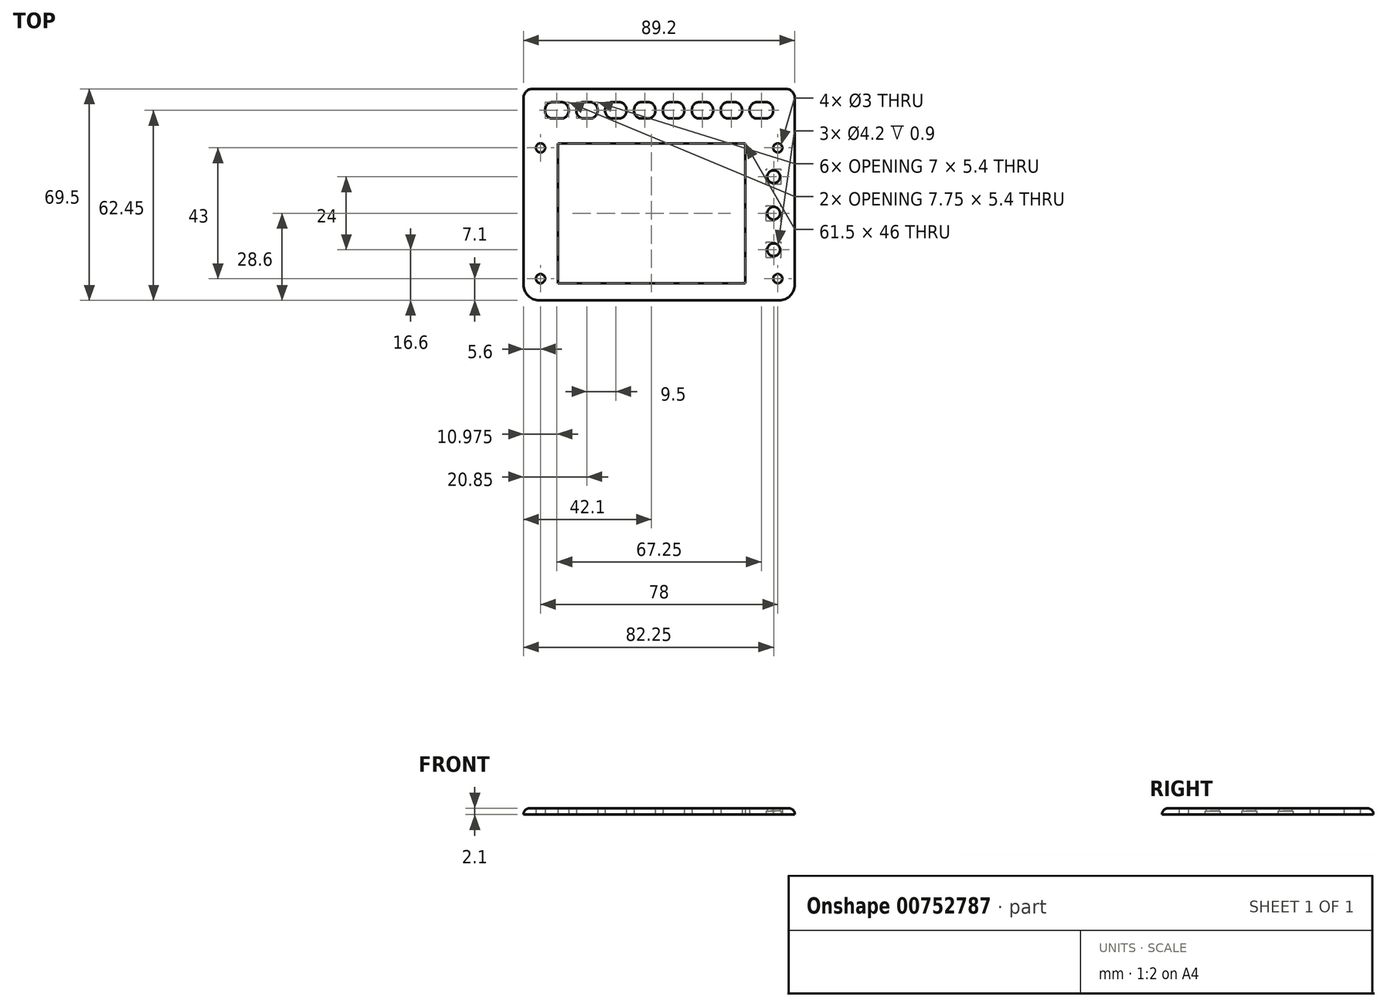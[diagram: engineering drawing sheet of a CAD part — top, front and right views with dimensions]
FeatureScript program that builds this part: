
annotation { "Feature Type Name" : "Feature", "Feature Type Description" : "" }
export const myFeature = defineFeature(function(context is Context, id is Id, definition is map)
    precondition{}
    {
        {
            var Q0;
            Q0=qCreatedBy(makeId("Top.planeOp"),FACE);
            var sketch = newSketch(context, id + "F0", { "sketchPlane" : qUnion([Q0])});
            skLineSegment(sketch, "E0.bottom", {"start": v(-39.5, 26.5) * mm, "end": v(39.5, 26.5) * mm});
            skLineSegment(sketch, "E0.top", {"start": v(-39.5, -26.5) * mm, "end": v(39.5, -26.5) * mm});
            skLineSegment(sketch, "E0.left", {"start": v(-42.5, 23.5) * mm, "end": v(-42.5, -23.5) * mm});
            skLineSegment(sketch, "E0.right", {"start": v(42.5, 23.5) * mm, "end": v(42.5, -23.5) * mm});
            skPoint(sketch, "E0.middle", {"position": v(0, 0) * mm});
            skLineSegment(sketch, "E1.bottom", {"start": v(-39, 21.5) * mm, "end": v(39, 21.5) * mm, "construction": true});
            skLineSegment(sketch, "E1.top", {"start": v(-39, -21.5) * mm, "end": v(39, -21.5) * mm, "construction": true});
            skLineSegment(sketch, "E1.left", {"start": v(-39, 21.5) * mm, "end": v(-39, -21.5) * mm, "construction": true});
            skLineSegment(sketch, "E1.right", {"start": v(39, 21.5) * mm, "end": v(39, -21.5) * mm, "construction": true});
            skCircle(sketch, "E2", {"center": v(-39, 21.5) * mm, "radius": 1.5 * mm});
            skCircle(sketch, "E3", {"center": v(39, 21.5) * mm, "radius": 1.5 * mm});
            skCircle(sketch, "E4", {"center": v(39, -21.5) * mm, "radius": 1.5 * mm});
            skCircle(sketch, "E5", {"center": v(-39, -21.5) * mm, "radius": 1.5 * mm});
            skPoint(sketch, "E6.visualSharp", {"position": v(-42.5, 26.5) * mm});
            skArc(sketch, "E6.filletArc", {"start": v(-39.5, 26.5) * mm, "mid": v(-41.62, 25.62) * mm, "end": v(-42.5, 23.5) * mm});
            skPoint(sketch, "E7.visualSharp", {"position": v(42.5, 26.5) * mm});
            skArc(sketch, "E7.filletArc", {"start": v(42.5, 23.5) * mm, "mid": v(41.62, 25.62) * mm, "end": v(39.5, 26.5) * mm});
            skPoint(sketch, "E8.visualSharp", {"position": v(42.5, -26.5) * mm});
            skArc(sketch, "E8.filletArc", {"start": v(39.5, -26.5) * mm, "mid": v(41.62, -25.62) * mm, "end": v(42.5, -23.5) * mm});
            skPoint(sketch, "E9.visualSharp", {"position": v(-42.5, -26.5) * mm});
            skArc(sketch, "E9.filletArc", {"start": v(-42.5, -23.5) * mm, "mid": v(-41.62, -25.62) * mm, "end": v(-39.5, -26.5) * mm});
            skLineSegment(sketch, "E10", {"start": v(0, 0) * mm, "end": v(-35, 0) * mm, "construction": true});
            skLineSegment(sketch, "E11", {"start": v(-35, 26.5) * mm, "end": v(-35, -26.5) * mm});
            skLineSegment(sketch, "E12", {"start": v(0, 0) * mm, "end": v(0, 23) * mm, "construction": true});
            skLineSegment(sketch, "E13.MirrorCS", {"start": v(35, 26.5) * mm, "end": v(35, -26.5) * mm});
            skLineSegment(sketch, "E14.1", {"start": v(-44.6, 23.5) * mm, "end": v(-44.6, -23.5) * mm});
            skLineSegment(sketch, "E14.2", {"start": v(-39.5, 28.6) * mm, "end": v(39.5, 28.6) * mm});
            skArc(sketch, "E14.3", {"start": v(-44.6, -23.5) * mm, "mid": v(-43.1, -27.1) * mm, "end": v(-39.5, -28.6) * mm});
            skLineSegment(sketch, "E14.5", {"start": v(44.6, 23.5) * mm, "end": v(44.6, -23.5) * mm});
            skArc(sketch, "E14.6", {"start": v(39.5, -28.6) * mm, "mid": v(43.1, -27.1) * mm, "end": v(44.6, -23.5) * mm});
            skLineSegment(sketch, "E14.7", {"start": v(-39.5, -28.6) * mm, "end": v(39.5, -28.6) * mm});
            skLineSegment(sketch, "E15", {"start": v(-42.5, 0) * mm, "end": v(-44.6, 0) * mm, "construction": true});
            skLineSegment(sketch, "E16.bottom", {"start": v(-44.6, 9) * mm, "end": v(-42.5, 9) * mm});
            skLineSegment(sketch, "E16.top", {"start": v(-44.6, -9) * mm, "end": v(-42.5, -9) * mm});
            skLineSegment(sketch, "E16.left", {"start": v(-44.6, 9) * mm, "end": v(-44.6, -9) * mm});
            skLineSegment(sketch, "E16.right", {"start": v(-42.5, 9) * mm, "end": v(-42.5, -9) * mm});
            skPoint(sketch, "E16.middle", {"position": v(-43.55, 0) * mm});
            skLineSegment(sketch, "E17", {"start": v(-42.5, 9) * mm, "end": v(-35, 9) * mm});
            skLineSegment(sketch, "E18", {"start": v(-42.5, -9) * mm, "end": v(-35, -9) * mm});
            skLineSegment(sketch, "E19", {"start": v(0, 28.6) * mm, "end": v(0, 39.1) * mm, "construction": true});
            skLineSegment(sketch, "E20", {"start": v(0, 39.1) * mm, "end": v(-39.5, 39.1) * mm});
            skLineSegment(sketch, "E21", {"start": v(0, 39.1) * mm, "end": v(39.5, 39.1) * mm});
            skLineSegment(sketch, "E22.0", {"start": v(0, 40.9) * mm, "end": v(41.6, 40.9) * mm});
            skLineSegment(sketch, "E22.1", {"start": v(0, 40.9) * mm, "end": v(-41.6, 40.9) * mm});
            skLineSegment(sketch, "E23", {"start": v(-42.5, 23.5) * mm, "end": v(-42.5, 36.1) * mm});
            skLineSegment(sketch, "E24", {"start": v(42.5, 23.5) * mm, "end": v(42.5, 36.1) * mm});
            skPoint(sketch, "E25.visualSharp", {"position": v(42.5, 39.1) * mm});
            skArc(sketch, "E25.filletArc", {"start": v(42.5, 36.1) * mm, "mid": v(41.62, 38.22) * mm, "end": v(39.5, 39.1) * mm});
            skPoint(sketch, "E26.visualSharp", {"position": v(-42.5, 39.1) * mm});
            skArc(sketch, "E26.filletArc", {"start": v(-39.5, 39.1) * mm, "mid": v(-41.62, 38.22) * mm, "end": v(-42.5, 36.1) * mm});
            skPoint(sketch, "E27.start.orphan", {"position": v(-44.6, 39.1) * mm});
            skPoint(sketch, "E28.start.orphan", {"position": v(44.6, 39.1) * mm});
            skLineSegment(sketch, "E29", {"start": v(-44.6, 23.5) * mm, "end": v(-44.6, 37.9) * mm});
            skLineSegment(sketch, "E30", {"start": v(44.6, 23.5) * mm, "end": v(44.6, 37.9) * mm});
            skPoint(sketch, "E31.visualSharp", {"position": v(-44.6, 40.9) * mm});
            skArc(sketch, "E31.filletArc", {"start": v(-41.6, 40.9) * mm, "mid": v(-43.72, 40.02) * mm, "end": v(-44.6, 37.9) * mm});
            skPoint(sketch, "E32.visualSharp", {"position": v(44.6, 40.9) * mm});
            skArc(sketch, "E32.filletArc", {"start": v(44.6, 37.9) * mm, "mid": v(43.72, 40.02) * mm, "end": v(41.6, 40.9) * mm});
            skLineSegment(sketch, "E33", {"start": v(-39.5, 28.6) * mm, "end": v(-42.5, 28.6) * mm});
            skLineSegment(sketch, "E34", {"start": v(39.5, 28.6) * mm, "end": v(42.5, 28.6) * mm});
            skEllipse(sketch, "E35", {"center": v(-39.5, 33.85) * mm, "majorRadius": 5.25 * mm, "minorRadius": 2.78 * mm, "majorAxis": v(0, 1)});
            skPoint(sketch, "E35.centerSnap0", {"position": v(0, 33.85) * mm});
            skLineSegment(sketch, "E36.bottom", {"start": v(-37.5, 31.15) * mm, "end": v(37.5, 31.15) * mm});
            skLineSegment(sketch, "E36.top", {"start": v(-37.5, 36.55) * mm, "end": v(37.5, 36.55) * mm});
            skLineSegment(sketch, "E36.left", {"start": v(-37.5, 31.15) * mm, "end": v(-37.5, 36.55) * mm});
            skLineSegment(sketch, "E36.right", {"start": v(37.5, 31.15) * mm, "end": v(37.5, 36.55) * mm});
            skLineSegment(sketch, "E37", {"start": v(0, 23) * mm, "end": v(-33.25, 23) * mm});
            skLineSegment(sketch, "E38", {"start": v(-33.25, 23) * mm, "end": v(-33.25, -23) * mm});
            skLineSegment(sketch, "E39", {"start": v(-33.25, -23) * mm, "end": v(28.25, -23) * mm});
            skLineSegment(sketch, "E40", {"start": v(28.25, -23) * mm, "end": v(28.25, 23) * mm});
            skLineSegment(sketch, "E41", {"start": v(28.25, 23) * mm, "end": v(0, 23) * mm});
            skLineSegment(sketch, "E42.bottom", {"start": v(-1.25, 36.55) * mm, "end": v(1.25, 36.55) * mm});
            skLineSegment(sketch, "E42.top", {"start": v(-1.25, 31.15) * mm, "end": v(1.25, 31.15) * mm});
            skLineSegment(sketch, "E42.left", {"start": v(-1.25, 36.55) * mm, "end": v(-1.25, 31.15) * mm});
            skLineSegment(sketch, "E42.right", {"start": v(1.25, 36.55) * mm, "end": v(1.25, 31.15) * mm});
            skLineSegment(sketch, "E43.1.0.0", {"start": v(10.75, 36.55) * mm, "end": v(10.75, 31.15) * mm});
            skLineSegment(sketch, "E43.1.0.1", {"start": v(8.25, 36.55) * mm, "end": v(8.25, 31.15) * mm});
            skLineSegment(sketch, "E43.2.0.0", {"start": v(20.25, 36.55) * mm, "end": v(20.25, 31.15) * mm});
            skLineSegment(sketch, "E43.2.0.1", {"start": v(17.75, 36.55) * mm, "end": v(17.75, 31.15) * mm});
            skLineSegment(sketch, "E43.3.0.0", {"start": v(29.75, 36.55) * mm, "end": v(29.75, 31.15) * mm});
            skLineSegment(sketch, "E43.3.0.1", {"start": v(27.25, 36.55) * mm, "end": v(27.25, 31.15) * mm});
            skLineSegment(sketch, "E43.direction1", {"start": v(1.25, 31.15) * mm, "end": v(10.75, 31.15) * mm, "construction": true});
            skLineSegment(sketch, "E44.1.0.0", {"start": v(-10.75, 36.55) * mm, "end": v(-10.75, 31.15) * mm});
            skLineSegment(sketch, "E44.1.0.1", {"start": v(-8.25, 36.55) * mm, "end": v(-8.25, 31.15) * mm});
            skLineSegment(sketch, "E44.1.0.2", {"start": v(-47, 31.15) * mm, "end": v(28, 31.15) * mm});
            skLineSegment(sketch, "E44.2.0.0", {"start": v(-20.25, 36.55) * mm, "end": v(-20.25, 31.15) * mm});
            skLineSegment(sketch, "E44.2.0.1", {"start": v(-17.75, 36.55) * mm, "end": v(-17.75, 31.15) * mm});
            skLineSegment(sketch, "E44.2.0.2", {"start": v(-56.5, 31.15) * mm, "end": v(18.5, 31.15) * mm});
            skLineSegment(sketch, "E44.3.0.0", {"start": v(-29.75, 36.55) * mm, "end": v(-29.75, 31.15) * mm});
            skLineSegment(sketch, "E44.3.0.1", {"start": v(-27.25, 36.55) * mm, "end": v(-27.25, 31.15) * mm});
            skLineSegment(sketch, "E44.3.0.2", {"start": v(-66, 31.15) * mm, "end": v(9, 31.15) * mm});
            skLineSegment(sketch, "E44.direction1", {"start": v(-1.25, 31.15) * mm, "end": v(-10.75, 31.15) * mm, "construction": true});
            skLineSegment(sketch, "E45", {"start": v(42.5, 0) * mm, "end": v(37.65, 0) * mm, "construction": true});
            skCircle(sketch, "E46", {"center": v(37.65, 0) * mm, "radius": 2.1 * mm});
            skCircle(sketch, "E47.0.1.0", {"center": v(37.65, 12) * mm, "radius": 2.1 * mm});
            skLineSegment(sketch, "E47.direction1", {"start": v(37.65, 0) * mm, "end": v(57.75, 0) * mm, "construction": true});
            skLineSegment(sketch, "E47.direction2", {"start": v(37.65, 0) * mm, "end": v(37.65, 12) * mm, "construction": true});
            skCircle(sketch, "E48.0.1.0", {"center": v(37.65, -12) * mm, "radius": 2.1 * mm});
            skLineSegment(sketch, "E48.direction1", {"start": v(37.65, 0) * mm, "end": v(62.65, 0) * mm, "construction": true});
            skLineSegment(sketch, "E48.direction2", {"start": v(37.65, 0) * mm, "end": v(37.65, -12) * mm, "construction": true});
            skLineSegment(sketch, "E49.bottom", {"start": v(40.15, 9.5) * mm, "end": v(35.15, 9.5) * mm});
            skLineSegment(sketch, "E49.top", {"start": v(40.15, 14.5) * mm, "end": v(35.15, 14.5) * mm});
            skLineSegment(sketch, "E49.left", {"start": v(40.15, 9.5) * mm, "end": v(40.15, 14.5) * mm});
            skLineSegment(sketch, "E49.right", {"start": v(35.15, 9.5) * mm, "end": v(35.15, 14.5) * mm});
            skLineSegment(sketch, "E50.bottom", {"start": v(35.15, -2.5) * mm, "end": v(40.15, -2.5) * mm});
            skLineSegment(sketch, "E50.top", {"start": v(35.15, 2.5) * mm, "end": v(40.15, 2.5) * mm});
            skLineSegment(sketch, "E50.left", {"start": v(35.15, -2.5) * mm, "end": v(35.15, 2.5) * mm});
            skLineSegment(sketch, "E50.right", {"start": v(40.15, -2.5) * mm, "end": v(40.15, 2.5) * mm});
            skLineSegment(sketch, "E51.bottom", {"start": v(35.15, -14.5) * mm, "end": v(40.15, -14.5) * mm});
            skLineSegment(sketch, "E51.top", {"start": v(35.15, -9.5) * mm, "end": v(40.15, -9.5) * mm});
            skLineSegment(sketch, "E51.left", {"start": v(35.15, -14.5) * mm, "end": v(35.15, -9.5) * mm});
            skLineSegment(sketch, "E51.right", {"start": v(40.15, -14.5) * mm, "end": v(40.15, -9.5) * mm});
            skSolve(sketch);
        }
        {
            var Q0;
            {var subQ3=sQuery(id+"F0.wireOp",EDGE,"E0.right");Q0=makeQuery(id+"F0.imprint","IMPRINT",FACE,{"disambiguationData":[TD([[makeQuery(id+"F0.imprint","IMPRINT",EDGE,{"derivedFrom":subQ3}),1.0]])]});}
            var Q1;
            Q1=makeQuery(id+"F0.imprint","IMPRINT",FACE,{"disambiguationData":[TD([[makeQuery(id+"F0.imprint","IMPRINT",EDGE,{"derivedFrom":sQuery(id+"F0.wireOp",EDGE,"E2")}),-1.0]])]});
            var Q2;
            Q2=makeQuery(id+"F0.imprint","IMPRINT",FACE,{"disambiguationData":[TD([[makeQuery(id+"F0.imprint","IMPRINT",EDGE,{"derivedFrom":sQuery(id+"F0.wireOp",EDGE,"E5")}),-1.0]])]});
            var Q3;
            Q3=makeQuery(id+"F0.imprint","IMPRINT",FACE,{"disambiguationData":[TD([[makeQuery(id+"F0.imprint","IMPRINT",EDGE,{"derivedFrom":sQuery(id+"F0.wireOp",EDGE,"E0.right")}),-1.0]])]});
            var Q4;
            {var subQ0=sQuery(id+"F0.wireOp",EDGE,"E6.filletArc");Q4=makeQuery(id+"F0.imprint","IMPRINT",FACE,{"disambiguationData":[TD([[makeQuery(id+"F0.imprint","IMPRINT",EDGE,{"derivedFrom":subQ0}),-1.0]])]});}
            var Q5;
            {var subQ43=sQuery(id+"F0.wireOp",EDGE,"E14.2");Q5=makeQuery(id+"F0.imprint","IMPRINT",FACE,{"disambiguationData":[TD([[makeQuery(id+"F0.imprint","IMPRINT",EDGE,{"derivedFrom":subQ43}),1.0]])]});}
            var Q6;
            {var subQ0=sQuery(id+"F0.wireOp",EDGE,"E6.filletArc");Q6=makeQuery(id+"F0.imprint","IMPRINT",FACE,{"disambiguationData":[TD([[makeQuery(id+"F0.imprint","IMPRINT",EDGE,{"derivedFrom":subQ0}),-1.0]])]});}
            var Q7;
            {var subQ3=sQuery(id+"F0.wireOp",EDGE,"E26.filletArc");Q7=makeQuery(id+"F0.imprint","IMPRINT",FACE,{"disambiguationData":[TD([[makeQuery(id+"F0.imprint","IMPRINT",EDGE,{"derivedFrom":subQ3}),1.0]])]});}
            var Q8;
            {var subQ0=sQuery(id+"F0.wireOp",EDGE,"E17");Q8=makeQuery(id+"F0.imprint","IMPRINT",FACE,{"disambiguationData":[TD([[makeQuery(id+"F0.imprint","IMPRINT",EDGE,{"derivedFrom":subQ0}),-1.0]])]});}
            var Q9;
            {var subQ0=sQuery(id+"F0.wireOp",EDGE,"E16.bottom");Q9=makeQuery(id+"F0.imprint","IMPRINT",FACE,{"disambiguationData":[TD([[makeQuery(id+"F0.imprint","IMPRINT",EDGE,{"derivedFrom":subQ0}),-1.0]])]});}
            var Q10;
            {var subQ0=sQuery(id+"F0.wireOp",EDGE,"E35");var subQ2=sQuery(id+"F0.wireOp",EDGE,"E44.1.0.2");var subQ3=makeQuery(id+"F0.imprint","INTERSECT",VERTEX,{"derivedFrom":[subQ0,subQ2]});Q10=makeQuery(id+"F0.imprint","IMPRINT",FACE,{"disambiguationData":[TD([[makeQuery(id+"F0.imprint","IMPRINT",EDGE,{"disambiguationData":[TD([[subQ3,-1.0]])],"derivedFrom":subQ0}),1.0]])]});}
            var Q11;
            {var subQ0=sQuery(id+"F0.wireOp",EDGE,"E13.MirrorCS");Q11=makeQuery(id+"F0.imprint","IMPRINT",FACE,{"disambiguationData":[TD([[makeQuery(id+"F0.imprint","IMPRINT",EDGE,{"derivedFrom":subQ0}),-1.0]])]});}
            var Q12;
            {var subQ0=sQuery(id+"F0.wireOp",EDGE,"E44.3.0.0");Q12=makeQuery(id+"F0.imprint","IMPRINT",FACE,{"disambiguationData":[TD([[makeQuery(id+"F0.imprint","IMPRINT",EDGE,{"derivedFrom":subQ0}),1.0]])]});}
            var Q13;
            {var subQ0=sQuery(id+"F0.wireOp",EDGE,"E44.2.0.0");Q13=makeQuery(id+"F0.imprint","IMPRINT",FACE,{"disambiguationData":[TD([[makeQuery(id+"F0.imprint","IMPRINT",EDGE,{"derivedFrom":subQ0}),1.0]])]});}
            var Q14;
            {var subQ0=sQuery(id+"F0.wireOp",EDGE,"E44.1.0.0");Q14=makeQuery(id+"F0.imprint","IMPRINT",FACE,{"disambiguationData":[TD([[makeQuery(id+"F0.imprint","IMPRINT",EDGE,{"derivedFrom":subQ0}),1.0]])]});}
            var Q15;
            {var subQ0=sQuery(id+"F0.wireOp",EDGE,"E42.left");Q15=makeQuery(id+"F0.imprint","IMPRINT",FACE,{"disambiguationData":[TD([[makeQuery(id+"F0.imprint","IMPRINT",EDGE,{"derivedFrom":subQ0}),1.0]])]});}
            var Q16;
            {var subQ0=sQuery(id+"F0.wireOp",EDGE,"E43.1.0.0");Q16=makeQuery(id+"F0.imprint","IMPRINT",FACE,{"disambiguationData":[TD([[makeQuery(id+"F0.imprint","IMPRINT",EDGE,{"derivedFrom":subQ0}),-1.0]])]});}
            var Q17;
            {var subQ0=sQuery(id+"F0.wireOp",EDGE,"E43.2.0.0");Q17=makeQuery(id+"F0.imprint","IMPRINT",FACE,{"disambiguationData":[TD([[makeQuery(id+"F0.imprint","IMPRINT",EDGE,{"derivedFrom":subQ0}),-1.0]])]});}
            var Q18;
            {var subQ0=sQuery(id+"F0.wireOp",EDGE,"E43.3.0.0");Q18=makeQuery(id+"F0.imprint","IMPRINT",FACE,{"disambiguationData":[TD([[makeQuery(id+"F0.imprint","IMPRINT",EDGE,{"derivedFrom":subQ0}),-1.0]])]});}
            var Q19;
            {var subQ3=sQuery(id+"F0.wireOp",EDGE,"E36.left");Q19=makeQuery(id+"F0.imprint","IMPRINT",FACE,{"disambiguationData":[TD([[makeQuery(id+"F0.imprint","IMPRINT",EDGE,{"derivedFrom":subQ3}),1.0]])]});}
            var Q20;
            {var subQ3=sQuery(id+"F0.wireOp",EDGE,"E33");Q20=makeQuery(id+"F0.imprint","IMPRINT",FACE,{"disambiguationData":[TD([[makeQuery(id+"F0.imprint","IMPRINT",EDGE,{"derivedFrom":subQ3}),-1.0]])]});}
            var Q21;
            {var subQ0=sQuery(id+"F0.wireOp",EDGE,"E16.bottom");Q21=makeQuery(id+"F0.imprint","IMPRINT",FACE,{"disambiguationData":[TD([[makeQuery(id+"F0.imprint","IMPRINT",EDGE,{"derivedFrom":subQ0}),1.0]])]});}
            var Q22;
            Q22=makeQuery(id+"F0.imprint","IMPRINT",FACE,{"disambiguationData":[TD([[makeQuery(id+"F0.imprint","IMPRINT",EDGE,{"derivedFrom":sQuery(id+"F0.wireOp",EDGE,"E47.0.1.0")}),-1.0]])]});
            var Q23;
            Q23=makeQuery(id+"F0.imprint","IMPRINT",FACE,{"disambiguationData":[TD([[makeQuery(id+"F0.imprint","IMPRINT",EDGE,{"derivedFrom":sQuery(id+"F0.wireOp",EDGE,"E46")}),-1.0]])]});
            var Q24;
            Q24=makeQuery(id+"F0.imprint","IMPRINT",FACE,{"disambiguationData":[TD([[makeQuery(id+"F0.imprint","IMPRINT",EDGE,{"derivedFrom":sQuery(id+"F0.wireOp",EDGE,"E48.0.1.0")}),-1.0]])]});
            extrude(context, id + "F1", {"entities" : qUnion([Q0, Q1, Q2, Q3, Q4, Q5, Q6, Q7, Q8, Q9, Q10, Q11, Q12, Q13, Q14, Q15, Q16, Q17, Q18, Q19, Q20, Q21, Q22, Q23, Q24]), "depth" : 2.1 * mm, "offsetDistance" : 25 * mm});
        }
        {
            var Q0;
            Q0=makeQuery(id+"F1.opExtrude","CAP_EDGE",EDGE,{"disambiguationData":[OSD([sQuery(id+"F0.wireOp",EDGE,"E14.1"),sQuery(id+"F0.wireOp",EDGE,"E29")])],"isStart":false});
            fillet(context, id + "F2", {"entities" : qUnion([Q0]), "radius" : 2 * mm, "tangentPropagation" : true, "allowEdgeOverflow" : false});
        }
        {
            var Q0;
            Q0=makeQuery(id+"F1.opExtrude","SWEPT_EDGE",EDGE,{"disambiguationData":[OSD([sQuery(id+"F0.wireOp",EDGE,"E36.top"),sQuery(id+"F0.wireOp",EDGE,"E36.left")])]});
            var Q1;
            Q1=makeQuery(id+"F1.opExtrude","SWEPT_EDGE",EDGE,{"disambiguationData":[OSD([sQuery(id+"F0.wireOp",EDGE,"E36.top"),sQuery(id+"F0.wireOp",EDGE,"E44.3.0.1")])]});
            var Q2;
            Q2=makeQuery(id+"F1.opExtrude","SWEPT_EDGE",EDGE,{"disambiguationData":[OSD([sQuery(id+"F0.wireOp",EDGE,"E36.top"),sQuery(id+"F0.wireOp",EDGE,"E44.2.0.1")])]});
            var Q3;
            Q3=makeQuery(id+"F1.opExtrude","SWEPT_EDGE",EDGE,{"disambiguationData":[OSD([sQuery(id+"F0.wireOp",EDGE,"E36.top"),sQuery(id+"F0.wireOp",EDGE,"E44.1.0.1")])]});
            var Q4;
            Q4=makeQuery(id+"F1.opExtrude","SWEPT_EDGE",EDGE,{"disambiguationData":[OSD([sQuery(id+"F0.wireOp",EDGE,"E36.top"),sQuery(id+"F0.wireOp",EDGE,"E42.right")])]});
            var Q5;
            Q5=makeQuery(id+"F1.opExtrude","SWEPT_EDGE",EDGE,{"disambiguationData":[OSD([sQuery(id+"F0.wireOp",EDGE,"E36.top"),sQuery(id+"F0.wireOp",EDGE,"E43.1.0.0")])]});
            var Q6;
            Q6=makeQuery(id+"F1.opExtrude","SWEPT_EDGE",EDGE,{"disambiguationData":[OSD([sQuery(id+"F0.wireOp",EDGE,"E36.top"),sQuery(id+"F0.wireOp",EDGE,"E43.2.0.0")])]});
            var Q7;
            Q7=makeQuery(id+"F1.opExtrude","SWEPT_EDGE",EDGE,{"disambiguationData":[OSD([sQuery(id+"F0.wireOp",EDGE,"E36.top"),sQuery(id+"F0.wireOp",EDGE,"E43.3.0.0")])]});
            var Q8;
            Q8=makeQuery(id+"F1.opExtrude","SWEPT_EDGE",EDGE,{"disambiguationData":[OSD([sQuery(id+"F0.wireOp",EDGE,"E36.top"),sQuery(id+"F0.wireOp",EDGE,"E36.right")])]});
            var Q9;
            Q9=makeQuery(id+"F1.opExtrude","SWEPT_EDGE",EDGE,{"disambiguationData":[OSD([sQuery(id+"F0.wireOp",EDGE,"E36.top"),sQuery(id+"F0.wireOp",EDGE,"E43.3.0.1")])]});
            var Q10;
            Q10=makeQuery(id+"F1.opExtrude","SWEPT_EDGE",EDGE,{"disambiguationData":[OSD([sQuery(id+"F0.wireOp",EDGE,"E36.top"),sQuery(id+"F0.wireOp",EDGE,"E43.2.0.1")])]});
            var Q11;
            Q11=makeQuery(id+"F1.opExtrude","SWEPT_EDGE",EDGE,{"disambiguationData":[OSD([sQuery(id+"F0.wireOp",EDGE,"E36.top"),sQuery(id+"F0.wireOp",EDGE,"E43.1.0.1")])]});
            var Q12;
            Q12=makeQuery(id+"F1.opExtrude","SWEPT_EDGE",EDGE,{"disambiguationData":[OSD([sQuery(id+"F0.wireOp",EDGE,"E36.top"),sQuery(id+"F0.wireOp",EDGE,"E42.left")])]});
            var Q13;
            Q13=makeQuery(id+"F1.opExtrude","SWEPT_EDGE",EDGE,{"disambiguationData":[OSD([sQuery(id+"F0.wireOp",EDGE,"E36.top"),sQuery(id+"F0.wireOp",EDGE,"E44.1.0.0")])]});
            var Q14;
            Q14=makeQuery(id+"F1.opExtrude","SWEPT_EDGE",EDGE,{"disambiguationData":[OSD([sQuery(id+"F0.wireOp",EDGE,"E36.top"),sQuery(id+"F0.wireOp",EDGE,"E44.2.0.0")])]});
            var Q15;
            Q15=makeQuery(id+"F1.opExtrude","SWEPT_EDGE",EDGE,{"disambiguationData":[OSD([sQuery(id+"F0.wireOp",EDGE,"E36.top"),sQuery(id+"F0.wireOp",EDGE,"E44.3.0.0")])]});
            var Q16;
            Q16=makeQuery(id+"F1.opExtrude","SWEPT_EDGE",EDGE,{"disambiguationData":[OSD([sQuery(id+"F0.wireOp",EDGE,"E36.bottom"),sQuery(id+"F0.wireOp",EDGE,"E36.left"),sQuery(id+"F0.wireOp",EDGE,"E44.1.0.2")])]});
            var Q17;
            Q17=makeQuery(id+"F1.opExtrude","SWEPT_EDGE",EDGE,{"disambiguationData":[OSD([sQuery(id+"F0.wireOp",EDGE,"E36.bottom"),sQuery(id+"F0.wireOp",EDGE,"E44.3.0.1")])]});
            var Q18;
            Q18=makeQuery(id+"F1.opExtrude","SWEPT_EDGE",EDGE,{"disambiguationData":[OSD([sQuery(id+"F0.wireOp",EDGE,"E36.bottom"),sQuery(id+"F0.wireOp",EDGE,"E44.2.0.1")])]});
            var Q19;
            Q19=makeQuery(id+"F1.opExtrude","SWEPT_EDGE",EDGE,{"disambiguationData":[OSD([sQuery(id+"F0.wireOp",EDGE,"E36.bottom"),sQuery(id+"F0.wireOp",EDGE,"E44.1.0.1")])]});
            var Q20;
            Q20=makeQuery(id+"F1.opExtrude","SWEPT_EDGE",EDGE,{"disambiguationData":[OSD([sQuery(id+"F0.wireOp",EDGE,"E36.bottom"),sQuery(id+"F0.wireOp",EDGE,"E42.right")])]});
            var Q21;
            Q21=makeQuery(id+"F1.opExtrude","SWEPT_EDGE",EDGE,{"disambiguationData":[OSD([sQuery(id+"F0.wireOp",EDGE,"E36.bottom"),sQuery(id+"F0.wireOp",EDGE,"E43.1.0.0")])]});
            var Q22;
            Q22=makeQuery(id+"F1.opExtrude","SWEPT_EDGE",EDGE,{"disambiguationData":[OSD([sQuery(id+"F0.wireOp",EDGE,"E36.bottom"),sQuery(id+"F0.wireOp",EDGE,"E43.3.0.0")])]});
            var Q23;
            Q23=makeQuery(id+"F1.opExtrude","SWEPT_EDGE",EDGE,{"disambiguationData":[OSD([sQuery(id+"F0.wireOp",EDGE,"E36.bottom"),sQuery(id+"F0.wireOp",EDGE,"E43.2.0.0")])]});
            var Q24;
            Q24=makeQuery(id+"F1.opExtrude","SWEPT_EDGE",EDGE,{"disambiguationData":[OSD([sQuery(id+"F0.wireOp",EDGE,"E36.bottom"),sQuery(id+"F0.wireOp",EDGE,"E36.right")])]});
            var Q25;
            Q25=makeQuery(id+"F1.opExtrude","SWEPT_EDGE",EDGE,{"disambiguationData":[OSD([sQuery(id+"F0.wireOp",EDGE,"E36.bottom"),sQuery(id+"F0.wireOp",EDGE,"E43.2.0.1")])]});
            var Q26;
            Q26=makeQuery(id+"F1.opExtrude","SWEPT_EDGE",EDGE,{"disambiguationData":[OSD([sQuery(id+"F0.wireOp",EDGE,"E36.bottom"),sQuery(id+"F0.wireOp",EDGE,"E43.3.0.1")])]});
            var Q27;
            Q27=makeQuery(id+"F1.opExtrude","SWEPT_EDGE",EDGE,{"disambiguationData":[OSD([sQuery(id+"F0.wireOp",EDGE,"E36.bottom"),sQuery(id+"F0.wireOp",EDGE,"E43.1.0.1")])]});
            var Q28;
            Q28=makeQuery(id+"F1.opExtrude","SWEPT_EDGE",EDGE,{"disambiguationData":[OSD([sQuery(id+"F0.wireOp",EDGE,"E36.bottom"),sQuery(id+"F0.wireOp",EDGE,"E42.left")])]});
            var Q29;
            Q29=makeQuery(id+"F1.opExtrude","SWEPT_EDGE",EDGE,{"disambiguationData":[OSD([sQuery(id+"F0.wireOp",EDGE,"E36.bottom"),sQuery(id+"F0.wireOp",EDGE,"E44.1.0.0")])]});
            var Q30;
            Q30=makeQuery(id+"F1.opExtrude","SWEPT_EDGE",EDGE,{"disambiguationData":[OSD([sQuery(id+"F0.wireOp",EDGE,"E36.bottom"),sQuery(id+"F0.wireOp",EDGE,"E44.2.0.0")])]});
            var Q31;
            Q31=makeQuery(id+"F1.opExtrude","SWEPT_EDGE",EDGE,{"disambiguationData":[OSD([sQuery(id+"F0.wireOp",EDGE,"E36.bottom"),sQuery(id+"F0.wireOp",EDGE,"E44.3.0.0")])]});
            fillet(context, id + "F3", {"entities" : qUnion([Q0, Q1, Q2, Q3, Q4, Q5, Q6, Q7, Q8, Q9, Q10, Q11, Q12, Q13, Q14, Q15, Q16, Q17, Q18, Q19, Q20, Q21, Q22, Q23, Q24, Q25, Q26, Q27, Q28, Q29, Q30, Q31]), "radius" : 2.5 * mm, "tangentPropagation" : true, "allowEdgeOverflow" : false});
        }
        {
            var Q0;
            Q0=makeQuery(id+"F0.imprint","IMPRINT",FACE,{"disambiguationData":[TD([[makeQuery(id+"F0.imprint","IMPRINT",EDGE,{"derivedFrom":sQuery(id+"F0.wireOp",EDGE,"E47.0.1.0")}),-1.0]])]});
            var Q1;
            Q1=makeQuery(id+"F0.imprint","IMPRINT",FACE,{"disambiguationData":[TD([[makeQuery(id+"F0.imprint","IMPRINT",EDGE,{"derivedFrom":sQuery(id+"F0.wireOp",EDGE,"E46")}),-1.0]])]});
            var Q2;
            Q2=makeQuery(id+"F0.imprint","IMPRINT",FACE,{"disambiguationData":[TD([[makeQuery(id+"F0.imprint","IMPRINT",EDGE,{"derivedFrom":sQuery(id+"F0.wireOp",EDGE,"E48.0.1.0")}),-1.0]])]});
            extrude(context, id + "F4", {"entities" : qUnion([Q0, Q1, Q2]), "operationType" : NewBodyOperationType.REMOVE, "depth" : 1.2 * mm, "offsetDistance" : 25 * mm});
        }
    });
